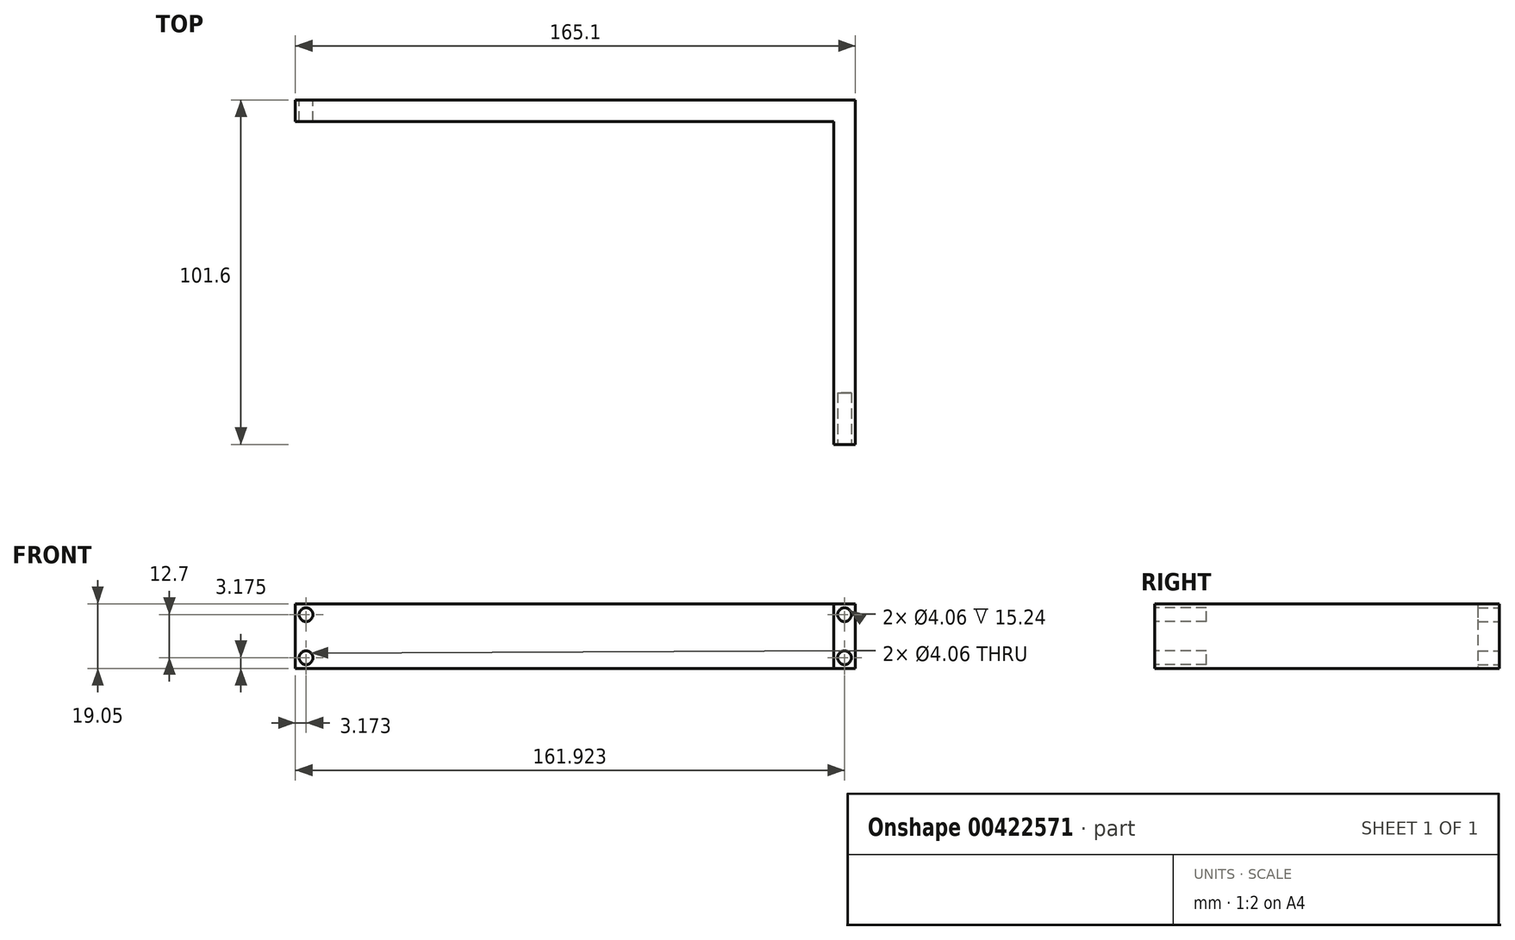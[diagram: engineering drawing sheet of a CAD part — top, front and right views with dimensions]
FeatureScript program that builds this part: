
annotation { "Feature Type Name" : "Feature", "Feature Type Description" : "" }
export const myFeature = defineFeature(function(context is Context, id is Id, definition is map)
    precondition{}
    {
        {
            var Q0;
            Q0=qCreatedBy(makeId("Top.planeOp"),FACE);
            var sketch = newSketch(context, id + "F0", { "sketchPlane" : qUnion([Q0])});
            skLineSegment(sketch, "E0.bottom", {"start": v(-87.12, 14.97) * mm, "end": v(77.98, 14.97) * mm});
            skLineSegment(sketch, "E0.top", {"start": v(-87.12, 8.62) * mm, "end": v(77.98, 8.62) * mm});
            skLineSegment(sketch, "E0.left", {"start": v(-87.12, 14.97) * mm, "end": v(-87.12, 8.62) * mm});
            skLineSegment(sketch, "E0.right", {"start": v(77.98, 14.97) * mm, "end": v(77.98, 8.62) * mm});
            skLineSegment(sketch, "E1.bottom", {"start": v(77.98, 14.97) * mm, "end": v(71.63, 14.97) * mm});
            skLineSegment(sketch, "E1.top", {"start": v(77.98, -86.63) * mm, "end": v(71.63, -86.63) * mm});
            skLineSegment(sketch, "E1.left", {"start": v(77.98, 14.97) * mm, "end": v(77.98, -86.63) * mm});
            skLineSegment(sketch, "E1.right", {"start": v(71.63, 14.97) * mm, "end": v(71.63, -86.63) * mm});
            skSolve(sketch);
        }
        {
            var Q0;
            {var subQ0=sQuery(id+"F0.wireOp",EDGE,"E0.bottom");Q0=makeQuery(id+"F0.imprint","IMPRINT",FACE,{"disambiguationData":[TD([[makeQuery(id+"F0.imprint","IMPRINT",EDGE,{"derivedFrom":subQ0}),-1.0]])]});}
            var Q1;
            {var subQ5=sQuery(id+"F0.wireOp",EDGE,"E1.bottom");Q1=makeQuery(id+"F0.imprint","IMPRINT",FACE,{"disambiguationData":[TD([[makeQuery(id+"F0.imprint","IMPRINT",EDGE,{"derivedFrom":subQ5}),1.0]])]});}
            var Q2;
            {var subQ5=sQuery(id+"F0.wireOp",EDGE,"E1.top");Q2=makeQuery(id+"F0.imprint","IMPRINT",FACE,{"disambiguationData":[TD([[makeQuery(id+"F0.imprint","IMPRINT",EDGE,{"derivedFrom":subQ5}),-1.0]])]});}
            extrude(context, id + "F1", {"entities" : qUnion([Q0, Q1, Q2]), "depth" : 19.05 * mm});
        }
        {
            var Q0;
            Q0=makeQuery(id+"F1.opExtrude","SWEPT_FACE",FACE,{"disambiguationData":[OSD([sQuery(id+"F0.wireOp",EDGE,"E1.top")])]});
            var sketch = newSketch(context, id + "F2", { "sketchPlane" : qUnion([Q0])});
            skCircle(sketch, "E2", {"center": v(74.8, 15.88) * mm, "radius": 2.03 * mm});
            skCircle(sketch, "E3", {"center": v(74.8, 3.18) * mm, "radius": 2.03 * mm});
            skLineSegment(sketch, "E4.0", {"start": v(77.98, 19.05) * mm, "end": v(71.63, 19.05) * mm, "construction": true});
            skLineSegment(sketch, "E5.0", {"start": v(77.98, 19.05) * mm, "end": v(77.98, 0) * mm, "construction": true});
            skSolve(sketch);
        }
        {
            var Q0;
            Q0 = qSketchRegion(id + "F2", true);
            extrude(context, id + "F3", {"entities" : qUnion([Q0]), "operationType" : NewBodyOperationType.REMOVE, "oppositeDirection" : true, "depth" : 15.24 * mm});
        }
        {
            var Q0;
            Q0=makeQuery(id+"F1.opExtrude","SWEPT_FACE",FACE,{"disambiguationData":[OSD([sQuery(id+"F0.wireOp",EDGE,"E0.bottom"),sQuery(id+"F0.wireOp",EDGE,"E1.bottom")])]});
            var sketch = newSketch(context, id + "F4", { "sketchPlane" : qUnion([Q0])});
            skCircle(sketch, "E6", {"center": v(83.95, 15.88) * mm, "radius": 2.03 * mm});
            skCircle(sketch, "E7", {"center": v(83.95, 3.18) * mm, "radius": 2.03 * mm});
            skSolve(sketch);
        }
        {
            var Q0;
            Q0 = qSketchRegion(id + "F4", true);
            extrude(context, id + "F5", {"entities" : qUnion([Q0]), "operationType" : NewBodyOperationType.REMOVE, "oppositeDirection" : true, "depth" : 25.4 * mm});
        }
    });
